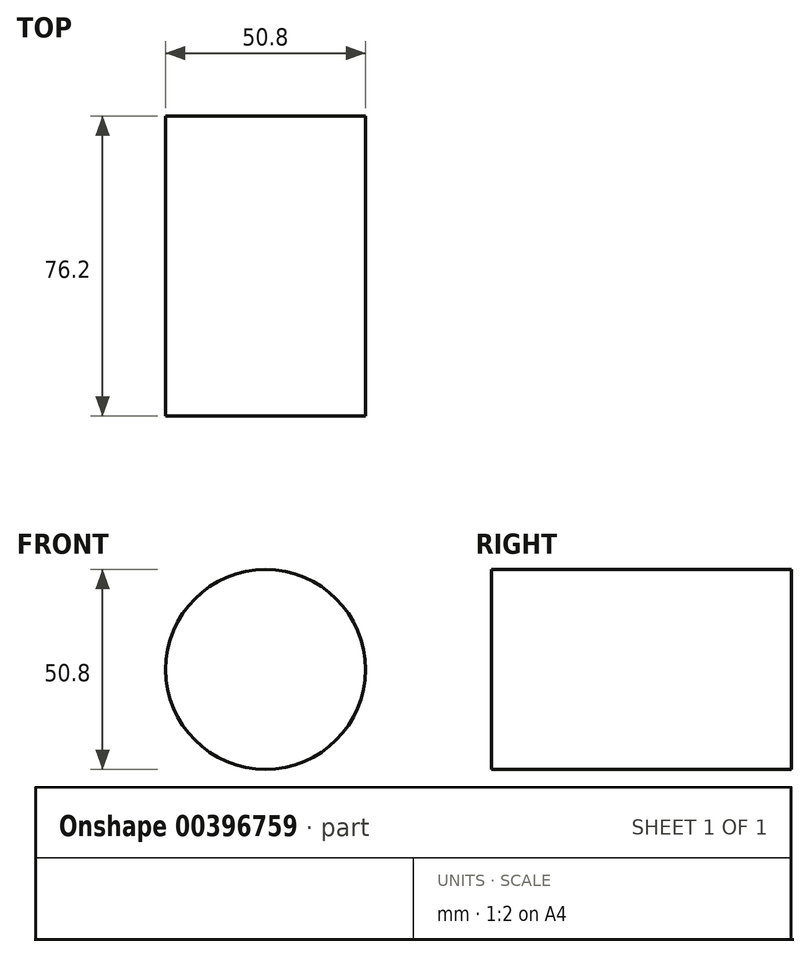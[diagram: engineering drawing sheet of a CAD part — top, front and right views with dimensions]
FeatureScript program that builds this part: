
annotation { "Feature Type Name" : "Feature", "Feature Type Description" : "" }
export const myFeature = defineFeature(function(context is Context, id is Id, definition is map)
    precondition{}
    {
        {
            var Q0;
            Q0=qCreatedBy(makeId("Front.planeOp"),FACE);
            var sketch = newSketch(context, id + "F0", { "sketchPlane" : qUnion([Q0])});
            skCircle(sketch, "E0", {"center": v(0, 0) * mm, "radius": 25.4 * mm});
            skSolve(sketch);
        }
        {
            var Q0;
            Q0 = qSketchRegion(id + "F0", true);
            extrude(context, id + "F1", {"entities" : qUnion([Q0]), "depth" : 101.6 * mm});
        }
        {
            var Q0;
            Q0=makeQuery(id+"F1.opExtrude","CAP_FACE",FACE,{"disambiguationData":[OSD([sQuery(id+"F0.wireOp",EDGE,"E0")])],"isStart":false});
            var sketch = newSketch(context, id + "F2", { "sketchPlane" : qUnion([Q0])});
            skCircle(sketch, "E1", {"center": v(0, 0) * mm, "radius": 20.47 * mm});
            skSolve(sketch);
        }
        {
            var Q0;
            Q0=makeQuery(id+"F2.imprint","IMPRINT",FACE,{"disambiguationData":[TD([[makeQuery(id+"F2.imprint","IMPRINT",EDGE,{"derivedFrom":sQuery(id+"F2.wireOp",EDGE,"E1")}),1.0]])]});
            var Q1;
            Q1=makeQuery(id+"F1.opExtrude","CAP_FACE",FACE,{"disambiguationData":[OSD([sQuery(id+"F0.wireOp",EDGE,"E0")])],"isStart":false});
            var Q2;
            Q2=makeQuery(id+"F1.opExtrude","CAP_FACE",FACE,{"disambiguationData":[OSD([sQuery(id+"F0.wireOp",EDGE,"E0")])],"isStart":true});
            extrude(context, id + "F3", {"entities" : qUnion([Q0, Q1, Q2]), "operationType" : NewBodyOperationType.REMOVE, "oppositeDirection" : true, "depth" : 25.4 * mm});
        }
    });
